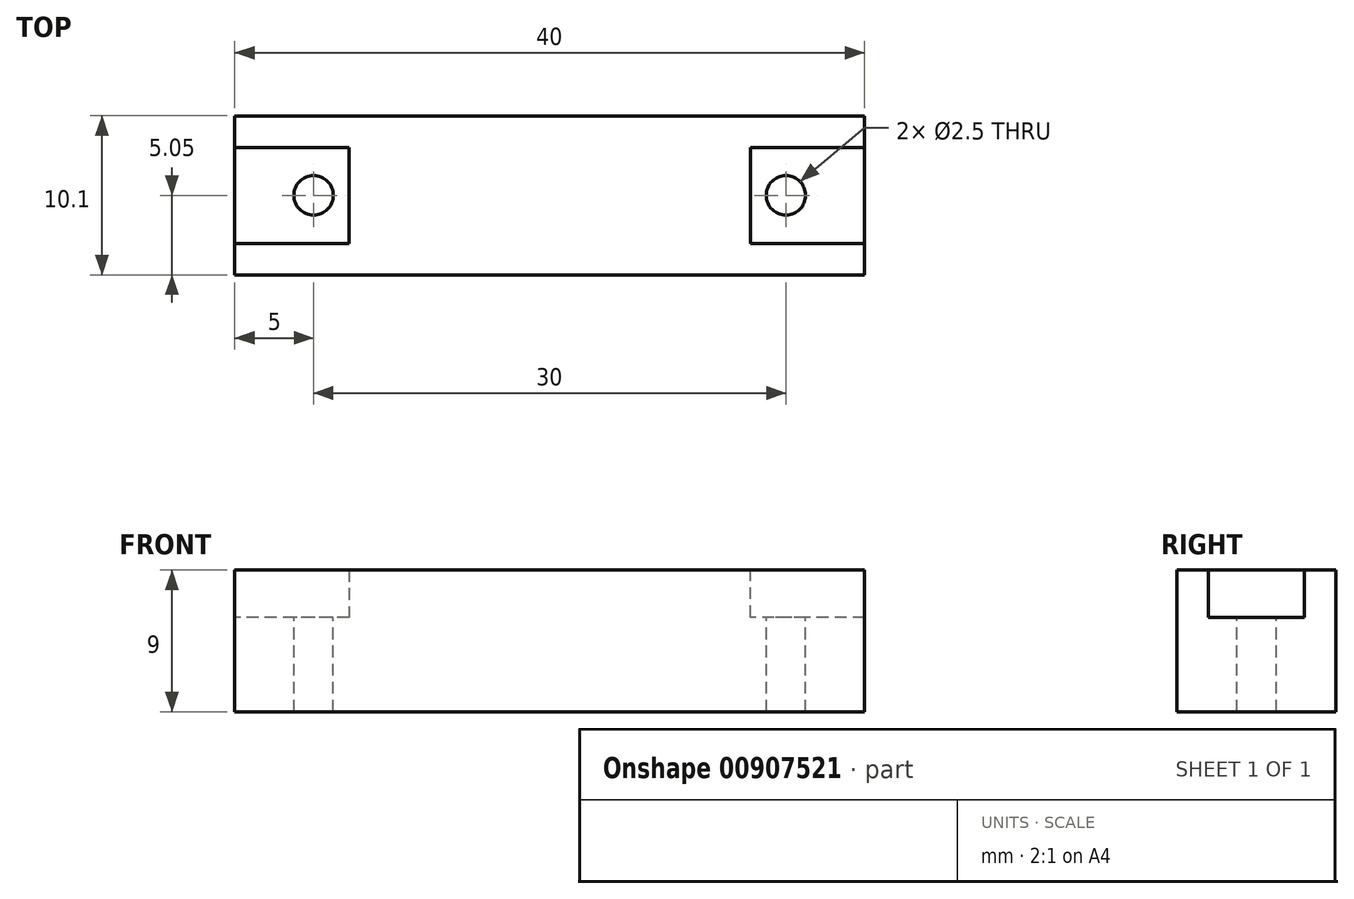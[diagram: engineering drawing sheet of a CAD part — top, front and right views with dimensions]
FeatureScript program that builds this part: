
annotation { "Feature Type Name" : "Feature", "Feature Type Description" : "" }
export const myFeature = defineFeature(function(context is Context, id is Id, definition is map)
    precondition{}
    {
        {
            var Q0;
            Q0=qCreatedBy(makeId("Front.planeOp"),FACE);
            var sketch = newSketch(context, id + "F0", { "sketchPlane" : qUnion([Q0])});
            skLineSegment(sketch, "E0", {"start": v(-20, 0) * mm, "end": v(-20, -6) * mm});
            skLineSegment(sketch, "E1", {"start": v(-20, -6) * mm, "end": v(20, -6) * mm});
            skLineSegment(sketch, "E2", {"start": v(20, -6) * mm, "end": v(20, 0) * mm});
            skLineSegment(sketch, "E3", {"start": v(20, 0) * mm, "end": v(12.75, 0) * mm});
            skLineSegment(sketch, "E4", {"start": v(12.75, 0) * mm, "end": v(12.75, 3) * mm});
            skLineSegment(sketch, "E5", {"start": v(12.75, 3) * mm, "end": v(-12.75, 3) * mm});
            skLineSegment(sketch, "E6", {"start": v(-12.75, 3) * mm, "end": v(-12.75, 0) * mm});
            skLineSegment(sketch, "E7", {"start": v(-12.75, 0) * mm, "end": v(-20, 0) * mm});
            skSolve(sketch);
        }
        {
            var Q0;
            Q0 = qSketchRegion(id + "F0", true);
            extrude(context, id + "F1", {"entities" : qUnion([Q0]), "endBound" : BoundingType.SYMMETRIC, "depth" : 6.1 * mm, "offsetDistance" : 25.4 * mm});
        }
        {
            var Q0;
            Q0=makeQuery(id+"F1.opExtrude","CAP_FACE",FACE,{"disambiguationData":[OSD([sQuery(id+"F0.wireOp",EDGE,"E0"),sQuery(id+"F0.wireOp",EDGE,"E1"),sQuery(id+"F0.wireOp",EDGE,"E2"),sQuery(id+"F0.wireOp",EDGE,"E3"),sQuery(id+"F0.wireOp",EDGE,"E4"),sQuery(id+"F0.wireOp",EDGE,"E5"),sQuery(id+"F0.wireOp",EDGE,"E6"),sQuery(id+"F0.wireOp",EDGE,"E7")])],"isStart":false});
            var sketch = newSketch(context, id + "F2", { "sketchPlane" : qUnion([Q0])});
            skLineSegment(sketch, "E8.bottom", {"start": v(-20, -6) * mm, "end": v(20, -6) * mm});
            skLineSegment(sketch, "E8.top", {"start": v(-20, 3) * mm, "end": v(20, 3) * mm});
            skLineSegment(sketch, "E8.left", {"start": v(-20, -6) * mm, "end": v(-20, 3) * mm});
            skLineSegment(sketch, "E8.right", {"start": v(20, -6) * mm, "end": v(20, 3) * mm});
            skSolve(sketch);
        }
        {
            var Q0;
            Q0 = qSketchRegion(id + "F2", true);
            extrude(context, id + "F3", {"entities" : qUnion([Q0]), "operationType" : NewBodyOperationType.ADD, "depth" : 2 * mm, "offsetDistance" : 25.4 * mm});
        }
        {
            var Q0;
            Q0=makeQuery(id+"F1.opExtrude","CAP_FACE",FACE,{"disambiguationData":[OSD([sQuery(id+"F0.wireOp",EDGE,"E0"),sQuery(id+"F0.wireOp",EDGE,"E1"),sQuery(id+"F0.wireOp",EDGE,"E2"),sQuery(id+"F0.wireOp",EDGE,"E3"),sQuery(id+"F0.wireOp",EDGE,"E4"),sQuery(id+"F0.wireOp",EDGE,"E5"),sQuery(id+"F0.wireOp",EDGE,"E6"),sQuery(id+"F0.wireOp",EDGE,"E7")])],"isStart":true});
            var sketch = newSketch(context, id + "F4", { "sketchPlane" : qUnion([Q0])});
            skLineSegment(sketch, "E9.bottom", {"start": v(-20, -6) * mm, "end": v(20, -6) * mm});
            skLineSegment(sketch, "E9.top", {"start": v(-20, 3) * mm, "end": v(20, 3) * mm});
            skLineSegment(sketch, "E9.left", {"start": v(-20, -6) * mm, "end": v(-20, 3) * mm});
            skLineSegment(sketch, "E9.right", {"start": v(20, -6) * mm, "end": v(20, 3) * mm});
            skSolve(sketch);
        }
        {
            var Q0;
            Q0 = qSketchRegion(id + "F4", true);
            extrude(context, id + "F5", {"entities" : qUnion([Q0]), "operationType" : NewBodyOperationType.ADD, "depth" : 2 * mm, "offsetDistance" : 25.4 * mm});
        }
        {
            var Q0;
            Q0=makeQuery(id+"F1.opExtrude","SWEPT_FACE",FACE,{"disambiguationData":[OSD([sQuery(id+"F0.wireOp",EDGE,"E7")])]});
            var sketch = newSketch(context, id + "F6", { "sketchPlane" : qUnion([Q0])});
            skPoint(sketch, "E10", {"position": v(-15, 0) * mm});
            skPoint(sketch, "E10.positionSnap0", {"position": v(-16.38, -3.05) * mm});
            skPoint(sketch, "E11", {"position": v(15, 0) * mm});
            skSolve(sketch);
        }
        {
            var Q0;
            Q0=sQuery(id+"F6.wireOp",VERTEX,"E10");
            var Q1;
            Q1=sQuery(id+"F6.wireOp",VERTEX,"E11");
            var Q2;
            Q2=makeQuery(id+"F1.opExtrude","SWEPT_BODY",BODY,{"disambiguationData":[OSD([sQuery(id+"F0.wireOp",EDGE,"E0"),sQuery(id+"F0.wireOp",EDGE,"E1"),sQuery(id+"F0.wireOp",EDGE,"E2"),sQuery(id+"F0.wireOp",EDGE,"E3"),sQuery(id+"F0.wireOp",EDGE,"E4"),sQuery(id+"F0.wireOp",EDGE,"E5"),sQuery(id+"F0.wireOp",EDGE,"E6"),sQuery(id+"F0.wireOp",EDGE,"E7")])]});
            hole(context, id + "F7", {"style" : HoleStyle.SIMPLE, "endStyle" : HoleEndStyle.THROUGH, "holeDiameter" : 2.5 * mm, "majorDiameter" : 6.35 * mm, "isTappedThrough" : true, "tappedDepth" : 9.52 * mm, "tapClearance" : 3, "locations" : qUnion([Q0, Q1]), "scope" : qUnion([Q2])});
        }
    });
